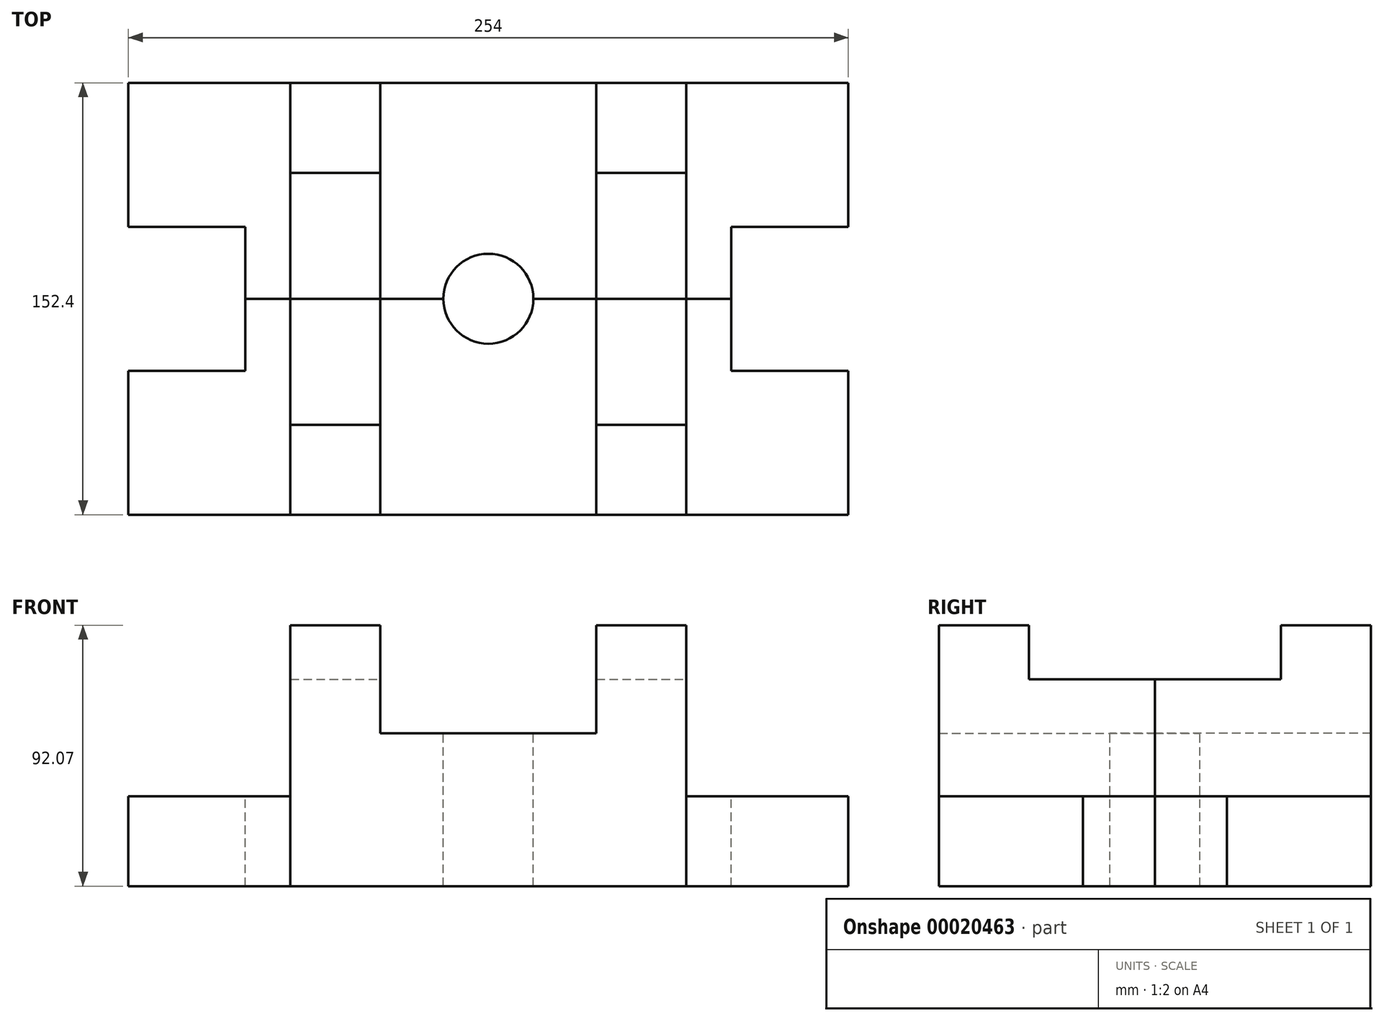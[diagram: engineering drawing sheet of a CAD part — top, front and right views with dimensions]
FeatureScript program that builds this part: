
annotation { "Feature Type Name" : "Feature", "Feature Type Description" : "" }
export const myFeature = defineFeature(function(context is Context, id is Id, definition is map)
    precondition{}
    {
        {
            var Q0;
            Q0=qCreatedBy(makeId("Front.planeOp"),FACE);
            var sketch = newSketch(context, id + "F0", { "sketchPlane" : qUnion([Q0])});
            skLineSegment(sketch, "E0.bottom", {"start": v(-3.23, 26.5) * mm, "end": v(104.72, 26.5) * mm});
            skLineSegment(sketch, "E0.top", {"start": v(-34.98, -65.58) * mm, "end": v(104.72, -65.58) * mm});
            skLineSegment(sketch, "E1", {"start": v(-34.98, 26.5) * mm, "end": v(-34.98, -65.58) * mm});
            skLineSegment(sketch, "E2", {"start": v(-3.23, 26.5) * mm, "end": v(-3.23, -65.58) * mm});
            skLineSegment(sketch, "E3", {"start": v(72.97, 26.5) * mm, "end": v(72.97, -65.58) * mm});
            skLineSegment(sketch, "E4", {"start": v(-34.98, 26.5) * mm, "end": v(-3.23, 26.5) * mm});
            skLineSegment(sketch, "E5", {"start": v(104.72, 26.5) * mm, "end": v(104.72, -65.58) * mm});
            skLineSegment(sketch, "E6", {"start": v(-3.23, -11.6) * mm, "end": v(72.97, -11.6) * mm});
            skLineSegment(sketch, "E7.bottom", {"start": v(104.72, -65.58) * mm, "end": v(161.87, -65.58) * mm});
            skLineSegment(sketch, "E7.top", {"start": v(104.72, -33.83) * mm, "end": v(161.87, -33.83) * mm});
            skLineSegment(sketch, "E7.left", {"start": v(104.72, -65.58) * mm, "end": v(104.72, -33.83) * mm});
            skLineSegment(sketch, "E7.right", {"start": v(161.87, -65.58) * mm, "end": v(161.87, -33.83) * mm});
            skLineSegment(sketch, "E8.bottom", {"start": v(-34.98, -65.58) * mm, "end": v(-92.13, -65.58) * mm});
            skLineSegment(sketch, "E8.top", {"start": v(-34.98, -33.83) * mm, "end": v(-92.13, -33.83) * mm});
            skLineSegment(sketch, "E8.left", {"start": v(-34.98, -65.58) * mm, "end": v(-34.98, -33.83) * mm});
            skLineSegment(sketch, "E8.right", {"start": v(-92.13, -65.58) * mm, "end": v(-92.13, -33.83) * mm});
            skSolve(sketch);
        }
        {
            var Q0;
            {var subQ0=sQuery(id+"F0.wireOp",EDGE,"E5");Q0=makeQuery(id+"F0.imprint","IMPRINT",FACE,{"disambiguationData":[TD([[makeQuery(id+"F0.imprint","IMPRINT",EDGE,{"derivedFrom":subQ0}),-1.0]])]});}
            var Q1;
            {var subQ5=sQuery(id+"F0.wireOp",EDGE,"E1");Q1=makeQuery(id+"F0.imprint","IMPRINT",FACE,{"disambiguationData":[TD([[makeQuery(id+"F0.imprint","IMPRINT",EDGE,{"derivedFrom":subQ5}),1.0]])]});}
            var Q2;
            {var subQ0=sQuery(id+"F0.wireOp",EDGE,"E6");Q2=makeQuery(id+"F0.imprint","IMPRINT",FACE,{"disambiguationData":[TD([[makeQuery(id+"F0.imprint","IMPRINT",EDGE,{"derivedFrom":subQ0}),1.0]])]});}
            var Q3;
            {var subQ1=sQuery(id+"F0.wireOp",EDGE,"E6");Q3=makeQuery(id+"F0.imprint","IMPRINT",FACE,{"disambiguationData":[TD([[makeQuery(id+"F0.imprint","IMPRINT",EDGE,{"derivedFrom":subQ1}),-1.0]])]});}
            extrude(context, id + "F1", {"entities" : qUnion([Q0, Q1, Q2, Q3]), "depth" : 76.2 * mm});
        }
        {
            var Q0;
            {var subQ0=sQuery(id+"F0.wireOp",EDGE,"E6");Q0=makeQuery(id+"F0.imprint","IMPRINT",FACE,{"disambiguationData":[TD([[makeQuery(id+"F0.imprint","IMPRINT",EDGE,{"derivedFrom":subQ0}),1.0]])]});}
            extrude(context, id + "F2", {"entities" : qUnion([Q0]), "operationType" : NewBodyOperationType.REMOVE, "depth" : 76.2 * mm});
        }
        {
            var Q0;
            Q0=makeQuery(id+"F0.imprint","IMPRINT",FACE,{"disambiguationData":[TD([[makeQuery(id+"F0.imprint","IMPRINT",EDGE,{"derivedFrom":sQuery(id+"F0.wireOp",EDGE,"E7.bottom")}),1.0]])]});
            var Q1;
            Q1=makeQuery(id+"F0.imprint","IMPRINT",FACE,{"disambiguationData":[TD([[makeQuery(id+"F0.imprint","IMPRINT",EDGE,{"derivedFrom":sQuery(id+"F0.wireOp",EDGE,"E8.bottom")}),-1.0]])]});
            extrude(context, id + "F3", {"entities" : qUnion([Q0, Q1]), "depth" : 76.2 * mm});
        }
        {
            var Q0;
            Q0=makeQuery(id+"F3.opExtrude","SWEPT_FACE",FACE,{"disambiguationData":[OSD([sQuery(id+"F0.wireOp",EDGE,"E7.top")])]});
            var sketch = newSketch(context, id + "F4", { "sketchPlane" : qUnion([Q0])});
            skLineSegment(sketch, "E9.bottom", {"start": v(161.87, 0) * mm, "end": v(120.6, 0) * mm});
            skLineSegment(sketch, "E9.top", {"start": v(161.87, -25.4) * mm, "end": v(120.6, -25.4) * mm});
            skLineSegment(sketch, "E9.left", {"start": v(161.87, 0) * mm, "end": v(161.87, -25.4) * mm});
            skLineSegment(sketch, "E9.right", {"start": v(120.6, 0) * mm, "end": v(120.6, -25.4) * mm});
            skSolve(sketch);
        }
        {
            var Q0;
            Q0=makeQuery(id+"F4.imprint","IMPRINT",FACE,{"disambiguationData":[TD([[makeQuery(id+"F4.imprint","IMPRINT",EDGE,{"derivedFrom":sQuery(id+"F4.wireOp",EDGE,"E9.bottom")}),-1.0]])]});
            extrude(context, id + "F5", {"entities" : qUnion([Q0]), "operationType" : NewBodyOperationType.REMOVE, "oppositeDirection" : true, "depth" : 31.75 * mm});
        }
        {
            var Q0;
            Q0=makeQuery(id+"F3.opExtrude","SWEPT_FACE",FACE,{"disambiguationData":[OSD([sQuery(id+"F0.wireOp",EDGE,"E8.top")])]});
            var sketch = newSketch(context, id + "F6", { "sketchPlane" : qUnion([Q0])});
            skLineSegment(sketch, "E10.bottom", {"start": v(-92.13, 0) * mm, "end": v(-50.85, 0) * mm});
            skLineSegment(sketch, "E10.top", {"start": v(-92.13, -25.4) * mm, "end": v(-50.85, -25.4) * mm});
            skLineSegment(sketch, "E10.left", {"start": v(-92.13, 0) * mm, "end": v(-92.13, -25.4) * mm});
            skLineSegment(sketch, "E10.right", {"start": v(-50.85, 0) * mm, "end": v(-50.85, -25.4) * mm});
            skSolve(sketch);
        }
        {
            var Q0;
            Q0=makeQuery(id+"F6.imprint","IMPRINT",FACE,{"disambiguationData":[TD([[makeQuery(id+"F6.imprint","IMPRINT",EDGE,{"derivedFrom":sQuery(id+"F6.wireOp",EDGE,"E10.bottom")}),1.0]])]});
            extrude(context, id + "F7", {"entities" : qUnion([Q0]), "operationType" : NewBodyOperationType.REMOVE, "oppositeDirection" : true, "depth" : 31.75 * mm});
        }
        {
            var Q0;
            {var subQ0=sQuery(id+"F0.wireOp",EDGE,"E0.bottom");var subQ1=sQuery(id+"F0.wireOp",EDGE,"E4");Q0=makeQuery(id+"F2.boolean.opBoolean","SPLIT",FACE,{"disambiguationData":[TD([makeQuery(id+"F2.opExtrude","SWEPT_FACE",FACE,{"disambiguationData":[OSD([sQuery(id+"F0.wireOp",EDGE,"E2")])]})])],"derivedFrom":makeQuery(id+"F1.opExtrude","SWEPT_FACE",FACE,{"disambiguationData":[OSD([subQ0,subQ1])]})});}
            var sketch = newSketch(context, id + "F8", { "sketchPlane" : qUnion([Q0])});
            skLineSegment(sketch, "E11.bottom", {"start": v(-34.98, 0) * mm, "end": v(-3.23, 0) * mm});
            skLineSegment(sketch, "E11.top", {"start": v(-34.98, -44.45) * mm, "end": v(-3.23, -44.45) * mm});
            skLineSegment(sketch, "E11.left", {"start": v(-34.98, 0) * mm, "end": v(-34.98, -44.45) * mm});
            skLineSegment(sketch, "E11.right", {"start": v(-3.23, 0) * mm, "end": v(-3.23, -44.45) * mm});
            skSolve(sketch);
        }
        {
            var Q0;
            Q0=makeQuery(id+"F8.imprint","IMPRINT",FACE,{"disambiguationData":[TD([[makeQuery(id+"F8.imprint","IMPRINT",EDGE,{"derivedFrom":sQuery(id+"F8.wireOp",EDGE,"E11.bottom")}),-1.0]])]});
            extrude(context, id + "F9", {"entities" : qUnion([Q0]), "operationType" : NewBodyOperationType.REMOVE, "oppositeDirection" : true, "depth" : 19.05 * mm});
        }
        {
            var Q0;
            {var subQ0=sQuery(id+"F0.wireOp",EDGE,"E0.bottom");var subQ1=sQuery(id+"F0.wireOp",EDGE,"E4");Q0=makeQuery(id+"F2.boolean.opBoolean","SPLIT",FACE,{"disambiguationData":[TD([makeQuery(id+"F2.opExtrude","SWEPT_FACE",FACE,{"disambiguationData":[OSD([sQuery(id+"F0.wireOp",EDGE,"E3")])]})])],"derivedFrom":makeQuery(id+"F1.opExtrude","SWEPT_FACE",FACE,{"disambiguationData":[OSD([subQ0,subQ1])]})});}
            var sketch = newSketch(context, id + "F10", { "sketchPlane" : qUnion([Q0])});
            skLineSegment(sketch, "E12.bottom", {"start": v(72.97, 0) * mm, "end": v(104.72, 0) * mm});
            skLineSegment(sketch, "E12.top", {"start": v(72.97, -44.45) * mm, "end": v(104.72, -44.45) * mm});
            skLineSegment(sketch, "E12.left", {"start": v(72.97, 0) * mm, "end": v(72.97, -44.45) * mm});
            skLineSegment(sketch, "E12.right", {"start": v(104.72, 0) * mm, "end": v(104.72, -44.45) * mm});
            skSolve(sketch);
        }
        {
            var Q0;
            Q0=makeQuery(id+"F10.imprint","IMPRINT",FACE,{"disambiguationData":[TD([[makeQuery(id+"F10.imprint","IMPRINT",EDGE,{"derivedFrom":sQuery(id+"F10.wireOp",EDGE,"E12.bottom")}),-1.0]])]});
            extrude(context, id + "F11", {"entities" : qUnion([Q0]), "operationType" : NewBodyOperationType.REMOVE, "oppositeDirection" : true, "depth" : 19.05 * mm});
        }
        {
            var Q0;
            Q0=makeQuery(id+"F2.boolean.opBoolean","COPY",FACE,{"derivedFrom":makeQuery(id+"F2.opExtrude","SWEPT_FACE",FACE,{"disambiguationData":[OSD([sQuery(id+"F0.wireOp",EDGE,"E6")])]})});
            var sketch = newSketch(context, id + "F12", { "sketchPlane" : qUnion([Q0])});
            skArc(sketch, "E13", {"start": v(19, 0) * mm, "mid": v(34.87, -15.88) * mm, "end": v(50.75, 0) * mm});
            skSolve(sketch);
        }
        {
            var Q0;
            Q0 = qSketchRegion(id + "F12", true);
            var Q1;
            {var subQ1=sQuery(id+"F12.wireOp",EDGE,"E13");Q1=makeQuery(id+"F12.imprint","IMPRINT",FACE,{"disambiguationData":[TD([[makeQuery(id+"F12.imprint","IMPRINT",EDGE,{"derivedFrom":subQ1}),1.0]])]});}
            extrude(context, id + "F13", {"entities" : qUnion([Q0, Q1]), "operationType" : NewBodyOperationType.REMOVE, "oppositeDirection" : true, "depth" : 60.32 * mm});
        }
        {
            var Q0;
            Q0=makeQuery(id+"F1.opExtrude","SWEPT_BODY",BODY,{"disambiguationData":[OSD([sQuery(id+"F0.wireOp",EDGE,"E0.bottom"),sQuery(id+"F0.wireOp",EDGE,"E0.top"),sQuery(id+"F0.wireOp",EDGE,"E1"),sQuery(id+"F0.wireOp",EDGE,"E4"),sQuery(id+"F0.wireOp",EDGE,"E5"),sQuery(id+"F0.wireOp",EDGE,"E7.left"),sQuery(id+"F0.wireOp",EDGE,"E8.left")])]});
            var Q1;
            Q1=makeQuery(id+"F3.opExtrude","SWEPT_BODY",BODY,{"disambiguationData":[OSD([sQuery(id+"F0.wireOp",EDGE,"E8.bottom"),sQuery(id+"F0.wireOp",EDGE,"E8.top"),sQuery(id+"F0.wireOp",EDGE,"E8.left"),sQuery(id+"F0.wireOp",EDGE,"E8.right")])]});
            var Q2;
            Q2=makeQuery(id+"F3.opExtrude","SWEPT_BODY",BODY,{"disambiguationData":[OSD([sQuery(id+"F0.wireOp",EDGE,"E7.bottom"),sQuery(id+"F0.wireOp",EDGE,"E7.top"),sQuery(id+"F0.wireOp",EDGE,"E7.left"),sQuery(id+"F0.wireOp",EDGE,"E7.right")])]});
            var Q3;
            {var subQ0=sQuery(id+"F0.wireOp",EDGE,"E5");Q3=makeQuery(id+"F0.imprint","IMPRINT",FACE,{"disambiguationData":[TD([[makeQuery(id+"F0.imprint","IMPRINT",EDGE,{"derivedFrom":subQ0}),-1.0]])]});}
            mirror(context, id + "F14", {"entities" : qUnion([Q0, Q1, Q2]), "mirrorPlane" : qUnion([Q3])});
        }
    });
